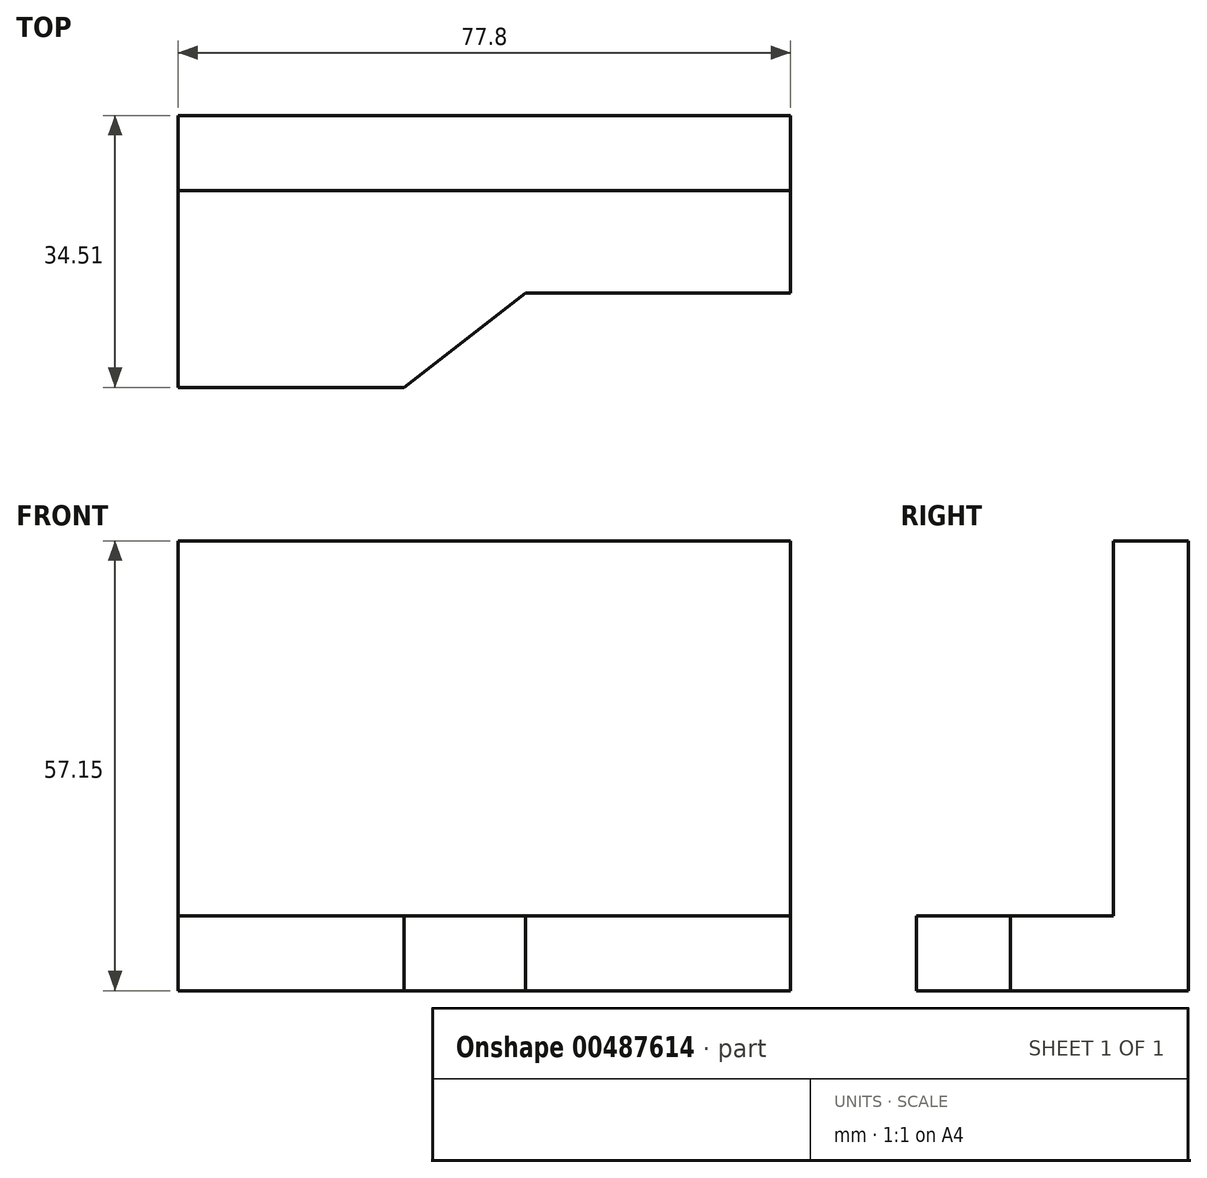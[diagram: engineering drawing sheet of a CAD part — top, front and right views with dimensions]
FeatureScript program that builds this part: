
annotation { "Feature Type Name" : "Feature", "Feature Type Description" : "" }
export const myFeature = defineFeature(function(context is Context, id is Id, definition is map)
    precondition{}
    {
        {
            var Q0;
            Q0=qCreatedBy(makeId("Front.planeOp"),FACE);
            var sketch = newSketch(context, id + "F0", { "sketchPlane" : qUnion([Q0])});
            skLineSegment(sketch, "E0.bottom", {"start": v(38.9, 23.81) * mm, "end": v(-38.9, 23.81) * mm});
            skLineSegment(sketch, "E0.top", {"start": v(38.9, -23.81) * mm, "end": v(-38.9, -23.81) * mm});
            skLineSegment(sketch, "E0.left", {"start": v(38.9, 23.81) * mm, "end": v(38.9, -23.81) * mm});
            skLineSegment(sketch, "E0.right", {"start": v(-38.9, 23.81) * mm, "end": v(-38.9, -23.81) * mm});
            skPoint(sketch, "E0.middle", {"position": v(0, 0) * mm});
            skSolve(sketch);
        }
        {
            var Q0;
            Q0 = qSketchRegion(id + "F0", true);
            var Q1;
            Q1=makeQuery(id+"F0.imprint","IMPRINT",FACE,{"disambiguationData":[TD([[makeQuery(id+"F0.imprint","IMPRINT",EDGE,{"derivedFrom":sQuery(id+"F0.wireOp",EDGE,"E0.bottom")}),1.0]])]});
            extrude(context, id + "F1", {"entities" : qUnion([Q0, Q1]), "depth" : 9.52 * mm});
        }
        {
            var Q0;
            Q0=makeQuery(id+"F1.opExtrude","CAP_FACE",FACE,{"disambiguationData":[OSD([sQuery(id+"F0.wireOp",EDGE,"E0.bottom"),sQuery(id+"F0.wireOp",EDGE,"E0.top"),sQuery(id+"F0.wireOp",EDGE,"E0.left"),sQuery(id+"F0.wireOp",EDGE,"E0.right")])],"isStart":false});
            var sketch = newSketch(context, id + "F2", { "sketchPlane" : qUnion([Q0])});
            skCircle(sketch, "E1", {"center": v(0, 0) * mm, "radius": 12.7 * mm});
            skSolve(sketch);
        }
        {
            var Q0;
            Q0=makeQuery(id+"F2.imprint","IMPRINT",FACE,{"disambiguationData":[TD([[makeQuery(id+"F2.imprint","IMPRINT",EDGE,{"derivedFrom":sQuery(id+"F2.wireOp",EDGE,"E1")}),1.0]])]});
            extrude(context, id + "F3", {"entities" : qUnion([Q0]), "operationType" : NewBodyOperationType.REMOVE, "depth" : 25.4 * mm});
        }
        {
            var Q0;
            Q0=makeQuery(id+"F1.opExtrude","SWEPT_FACE",FACE,{"disambiguationData":[OSD([sQuery(id+"F0.wireOp",EDGE,"E0.top")])]});
            var sketch = newSketch(context, id + "F4", { "sketchPlane" : qUnion([Q0])});
            skLineSegment(sketch, "E2", {"start": v(-38.9, 0) * mm, "end": v(38.9, 0) * mm});
            skLineSegment(sketch, "E3", {"start": v(38.9, 0) * mm, "end": v(38.9, 22.56) * mm});
            skLineSegment(sketch, "E4", {"start": v(38.9, 22.56) * mm, "end": v(5.2, 22.56) * mm});
            skLineSegment(sketch, "E5", {"start": v(5.2, 22.56) * mm, "end": v(-10.22, 34.51) * mm});
            skLineSegment(sketch, "E6", {"start": v(-38.9, 0) * mm, "end": v(-38.9, 34.51) * mm});
            skLineSegment(sketch, "E7", {"start": v(-38.9, 34.51) * mm, "end": v(-10.22, 34.51) * mm});
            skSolve(sketch);
        }
        {
            var Q0;
            {var subQ3=sQuery(id+"F4.wireOp",EDGE,"E4");Q0=makeQuery(id+"F4.imprint","IMPRINT",FACE,{"disambiguationData":[TD([[makeQuery(id+"F4.imprint","IMPRINT",EDGE,{"derivedFrom":subQ3}),1.0]])]});}
            var Q1;
            {var subQ0=sQuery(id+"F4.wireOp",EDGE,"E2");Q1=makeQuery(id+"F4.imprint","IMPRINT",FACE,{"disambiguationData":[TD([[makeQuery(id+"F4.imprint","IMPRINT",EDGE,{"derivedFrom":subQ0}),-1.0]])]});}
            extrude(context, id + "F5", {"entities" : qUnion([Q0, Q1]), "operationType" : NewBodyOperationType.ADD, "depth" : 9.52 * mm});
        }
    });
